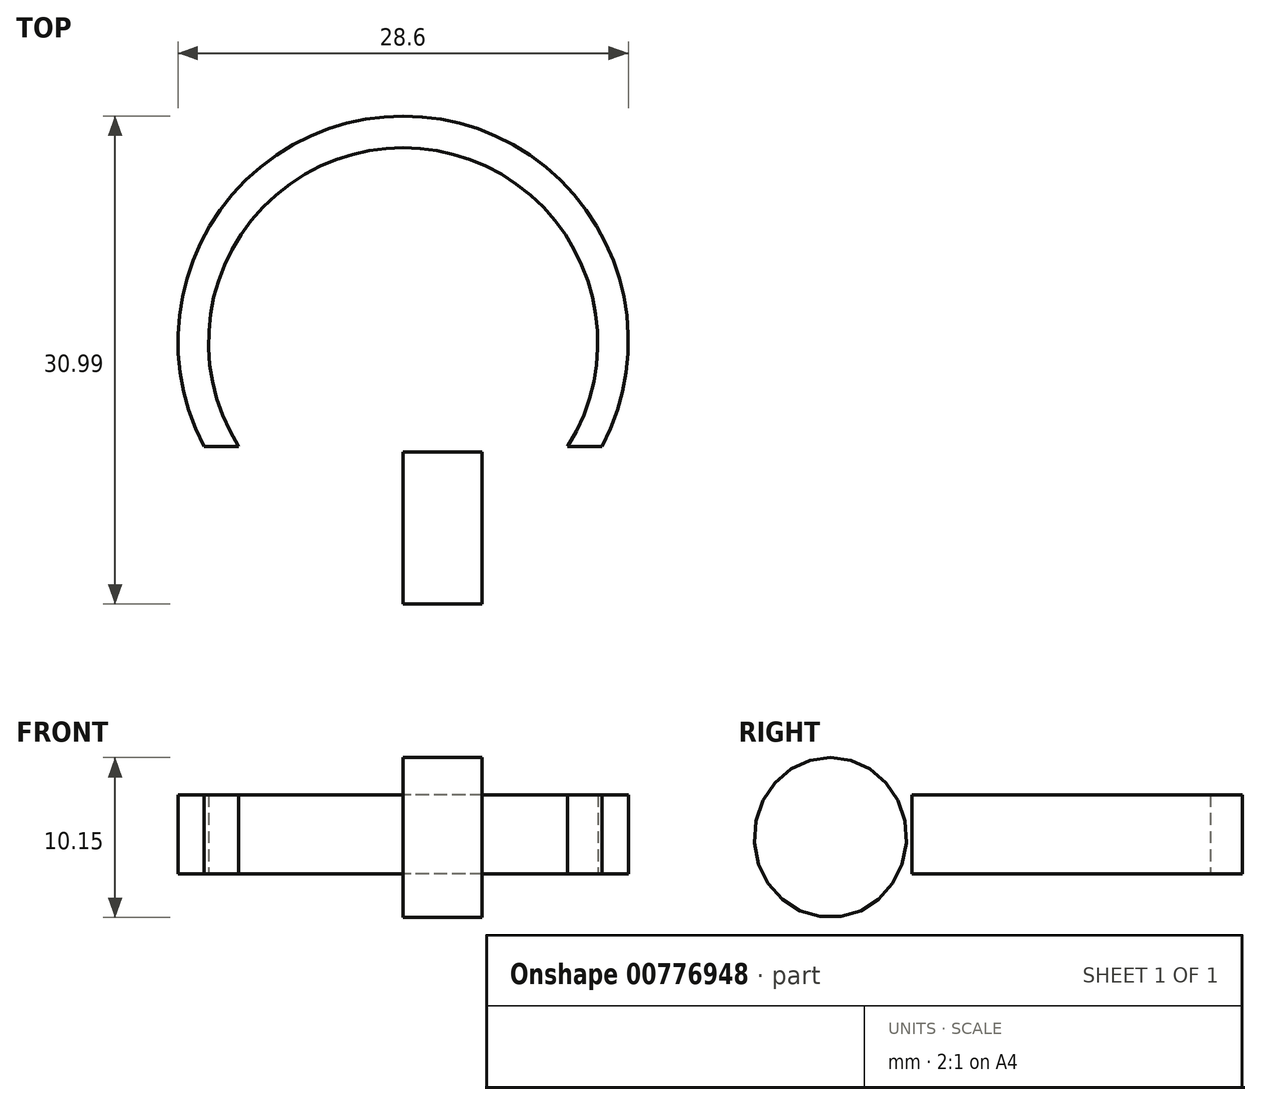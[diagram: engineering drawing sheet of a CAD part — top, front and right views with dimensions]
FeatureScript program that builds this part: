
annotation { "Feature Type Name" : "Feature", "Feature Type Description" : "" }
export const myFeature = defineFeature(function(context is Context, id is Id, definition is map)
    precondition{}
    {
        {
            var Q0;
            Q0=qCreatedBy(makeId("Top.planeOp"),FACE);
            var sketch = newSketch(context, id + "F0", { "sketchPlane" : qUnion([Q0])});
            skArc(sketch, "E0", {"start": v(10.44, 0) * mm, "mid": v(0, 18.98) * mm, "end": v(-10.44, 0) * mm});
            skArc(sketch, "E1", {"start": v(12.64, 0) * mm, "mid": v(0, 21) * mm, "end": v(-12.64, 0) * mm});
            skLineSegment(sketch, "E2", {"start": v(-12.64, 0) * mm, "end": v(-10.44, 0) * mm});
            skLineSegment(sketch, "E3", {"start": v(10.44, 0) * mm, "end": v(12.64, 0) * mm});
            skSolve(sketch);
        }
        {
            var Q0;
            Q0=makeQuery(id+"F0.imprint","IMPRINT",FACE,{"disambiguationData":[TD([[makeQuery(id+"F0.imprint","IMPRINT",EDGE,{"derivedFrom":sQuery(id+"F0.wireOp",EDGE,"E0")}),-1.0]])]});
            extrude(context, id + "F1", {"entities" : qUnion([Q0]), "depth" : 5 * mm, "offsetDistance" : 25.4 * mm});
        }
        {
            var Q0;
            Q0=qCreatedBy(makeId("Right.planeOp"),FACE);
            var sketch = newSketch(context, id + "F2", { "sketchPlane" : qUnion([Q0])});
            skEllipse(sketch, "E4", {"center": v(-5.17, 2.3) * mm, "majorRadius": 4.84 * mm, "minorRadius": 5.08 * mm, "majorAxis": v(1, 0)});
            skSolve(sketch);
        }
        {
            var Q0;
            Q0=makeQuery(id+"F2.imprint","IMPRINT",FACE,{"disambiguationData":[TD([[makeQuery(id+"F2.imprint","IMPRINT",EDGE,{"derivedFrom":sQuery(id+"F2.wireOp",EDGE,"E4")}),1.0]])]});
            extrude(context, id + "F3", {"entities" : qUnion([Q0]), "depth" : 5 * mm, "offsetDistance" : 25.4 * mm});
        }
    });
